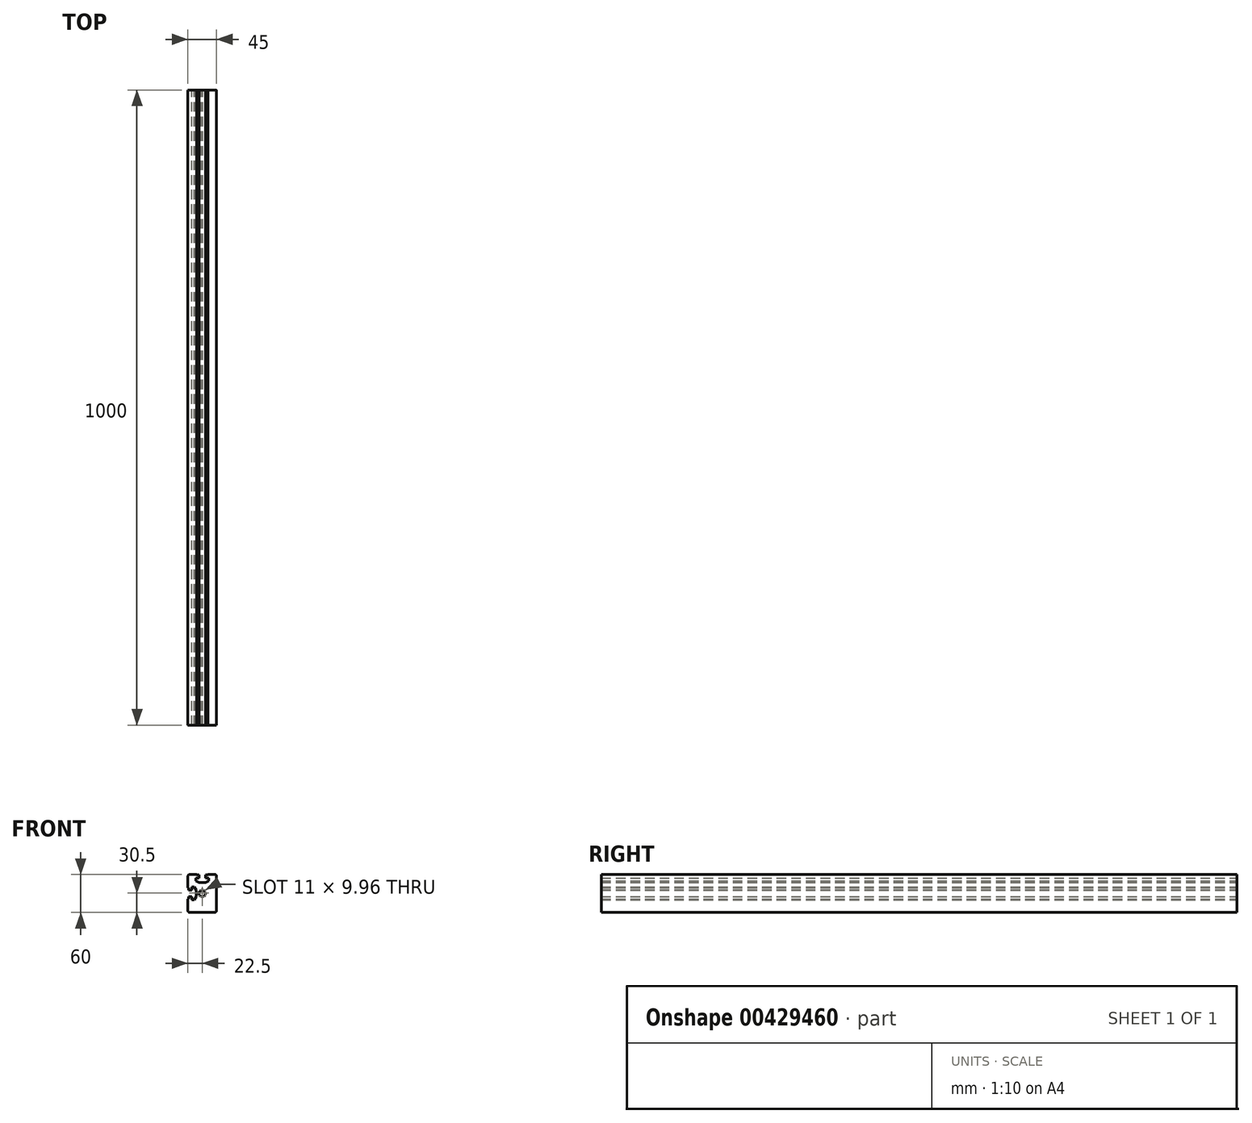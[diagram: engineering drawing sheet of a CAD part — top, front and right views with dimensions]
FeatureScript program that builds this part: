
annotation { "Feature Type Name" : "Feature", "Feature Type Description" : "" }
export const myFeature = defineFeature(function(context is Context, id is Id, definition is map)
    precondition{}
    {
        {
            var Q0;
            Q0=qCreatedBy(makeId("Front.planeOp"),FACE);
            var sketch = newSketch(context, id + "F0", { "sketchPlane" : qUnion([Q0])});
            skLineSegment(sketch, "E0.bottom", {"start": v(-22.5, 30) * mm, "end": v(22.5, 30) * mm});
            skLineSegment(sketch, "E0.top", {"start": v(-22.5, -30) * mm, "end": v(22.5, -30) * mm});
            skLineSegment(sketch, "E0.left", {"start": v(-22.5, 30) * mm, "end": v(-22.5, -30) * mm});
            skLineSegment(sketch, "E0.right", {"start": v(22.5, 30) * mm, "end": v(22.5, -30) * mm});
            skSolve(sketch);
        }
        {
            var Q0;
            Q0 = qSketchRegion(id + "F0", true);
            extrude(context, id + "F1", {"entities" : qUnion([Q0]), "depth" : 1000 * mm});
        }
        {
            var Q0;
            Q0=makeQuery(id+"F1.opExtrude","SWEPT_EDGE",EDGE,{"disambiguationData":[OSD([sQuery(id+"F0.wireOp",EDGE,"E0.top"),sQuery(id+"F0.wireOp",EDGE,"E0.left")])]});
            var Q1;
            Q1=makeQuery(id+"F1.opExtrude","SWEPT_EDGE",EDGE,{"disambiguationData":[OSD([sQuery(id+"F0.wireOp",EDGE,"E0.bottom"),sQuery(id+"F0.wireOp",EDGE,"E0.left")])]});
            var Q2;
            Q2=makeQuery(id+"F1.opExtrude","SWEPT_EDGE",EDGE,{"disambiguationData":[OSD([sQuery(id+"F0.wireOp",EDGE,"E0.top"),sQuery(id+"F0.wireOp",EDGE,"E0.right")])]});
            var Q3;
            Q3=makeQuery(id+"F1.opExtrude","SWEPT_EDGE",EDGE,{"disambiguationData":[OSD([sQuery(id+"F0.wireOp",EDGE,"E0.bottom"),sQuery(id+"F0.wireOp",EDGE,"E0.right")])]});
            fillet(context, id + "F2", {"entities" : qUnion([Q0, Q1, Q2, Q3]), "radius" : 3 * mm, "tangentPropagation" : true, "allowEdgeOverflow" : false});
        }
        {
            var Q0;
            Q0=qCreatedBy(makeId("Front.planeOp"),FACE);
            var sketch = newSketch(context, id + "F3", { "sketchPlane" : qUnion([Q0])});
            skCircle(sketch, "E1", {"center": v(0, 0) * mm, "radius": 5 * mm});
            skSolve(sketch);
        }
        {
            var Q0;
            Q0 = qSketchRegion(id + "F3", true);
            extrude(context, id + "F4", {"entities" : qUnion([Q0]), "operationType" : NewBodyOperationType.REMOVE, "endBound" : BoundingType.THROUGH_ALL, "depth" : 25 * mm});
        }
        {
            var Q0;
            Q0=qCreatedBy(makeId("Front.planeOp"),FACE);
            var sketch = newSketch(context, id + "F5", { "sketchPlane" : qUnion([Q0])});
            skLineSegment(sketch, "E2.bottom", {"start": v(-9, 30) * mm, "end": v(9, 30) * mm});
            skLineSegment(sketch, "E2.top", {"start": v(-9, 29) * mm, "end": v(-5, 29) * mm});
            skLineSegment(sketch, "E2.left", {"start": v(-9, 30) * mm, "end": v(-9, 29) * mm});
            skLineSegment(sketch, "E2.right", {"start": v(9, 30) * mm, "end": v(9, 29) * mm});
            skLineSegment(sketch, "E3.left", {"start": v(-5, 29) * mm, "end": v(-5, 24) * mm});
            skLineSegment(sketch, "E3.right", {"start": v(5, 29) * mm, "end": v(5, 24) * mm});
            skPoint(sketch, "E4.firstSnap0", {"position": v(0, 24) * mm});
            skLineSegment(sketch, "E4.bottom", {"start": v(-10.25, 24) * mm, "end": v(-5, 24) * mm});
            skLineSegment(sketch, "E4.top", {"start": v(-5.05, 17) * mm, "end": v(5.05, 17) * mm});
            skLineSegment(sketch, "E4.left", {"start": v(-10.25, 24) * mm, "end": v(-10.25, 20) * mm});
            skLineSegment(sketch, "E4.right", {"start": v(10.25, 24) * mm, "end": v(10.25, 20) * mm});
            skLineSegment(sketch, "E5.trimOffspring", {"start": v(5, 24) * mm, "end": v(10.25, 24) * mm});
            skLineSegment(sketch, "E6.trimOffspring", {"start": v(5, 29) * mm, "end": v(9, 29) * mm});
            skLineSegment(sketch, "E7", {"start": v(-10.25, 20) * mm, "end": v(-5.05, 17) * mm});
            skLineSegment(sketch, "E8", {"start": v(5.05, 17) * mm, "end": v(10.25, 20) * mm});
            skSolve(sketch);
        }
        {
            var Q0;
            Q0 = qSketchRegion(id + "F5", true);
            extrude(context, id + "F6", {"entities" : qUnion([Q0]), "operationType" : NewBodyOperationType.REMOVE, "endBound" : BoundingType.THROUGH_ALL, "depth" : 25 * mm});
        }
        {
            var Q0;
            Q0=qCreatedBy(makeId("Front.planeOp"),FACE);
            var sketch = newSketch(context, id + "F7", { "sketchPlane" : qUnion([Q0])});
            skLineSegment(sketch, "E9.bottom", {"start": v(-22.5, 9) * mm, "end": v(-21.5, 9) * mm});
            skLineSegment(sketch, "E9.top", {"start": v(-22.5, -9) * mm, "end": v(-21.5, -9) * mm});
            skLineSegment(sketch, "E9.left", {"start": v(-22.5, 9) * mm, "end": v(-22.5, -9) * mm});
            skLineSegment(sketch, "E9.right", {"start": v(-21.5, 9) * mm, "end": v(-21.5, 5) * mm});
            skLineSegment(sketch, "E10.bottom", {"start": v(-21.5, 5) * mm, "end": v(-16.5, 5) * mm});
            skLineSegment(sketch, "E10.top", {"start": v(-21.5, -5) * mm, "end": v(-16.5, -5) * mm});
            skLineSegment(sketch, "E11.bottom", {"start": v(-16.5, 10.25) * mm, "end": v(-12.5, 10.25) * mm});
            skLineSegment(sketch, "E11.top", {"start": v(-16.5, -10.25) * mm, "end": v(-12.5, -10.25) * mm});
            skLineSegment(sketch, "E11.left", {"start": v(-16.5, 10.25) * mm, "end": v(-16.5, 5) * mm});
            skLineSegment(sketch, "E11.right", {"start": v(-9.5, 5.05) * mm, "end": v(-9.5, -5.05) * mm});
            skLineSegment(sketch, "E12.trimOffspring", {"start": v(-16.5, -5) * mm, "end": v(-16.5, -10.25) * mm});
            skLineSegment(sketch, "E13.trimOffspring", {"start": v(-21.5, -5) * mm, "end": v(-21.5, -9) * mm});
            skLineSegment(sketch, "E14", {"start": v(-12.5, 10.25) * mm, "end": v(-9.5, 5.05) * mm});
            skLineSegment(sketch, "E15", {"start": v(-9.5, -5.05) * mm, "end": v(-12.5, -10.25) * mm});
            skSolve(sketch);
        }
        {
            var Q0;
            Q0 = qSketchRegion(id + "F7", true);
            extrude(context, id + "F8", {"entities" : qUnion([Q0]), "operationType" : NewBodyOperationType.REMOVE, "endBound" : BoundingType.THROUGH_ALL, "depth" : 25 * mm});
        }
        {
            var Q0;
            Q0=qCreatedBy(makeId("Front.planeOp"),FACE);
            var sketch = newSketch(context, id + "F9", { "sketchPlane" : qUnion([Q0])});
            skArc(sketch, "E16", {"start": v(1.04, 5.9) * mm, "mid": v(0, 6) * mm, "end": v(-1.04, 5.9) * mm});
            skLineSegment(sketch, "E17", {"start": v(-1.04, 5.9) * mm, "end": v(0, 0) * mm});
            skLineSegment(sketch, "E18", {"start": v(0, 0) * mm, "end": v(1.04, 5.9) * mm});
            skSolve(sketch);
        }
        {
            var Q0;
            Q0 = qSketchRegion(id + "F9", true);
            extrude(context, id + "F10", {"entities" : qUnion([Q0]), "operationType" : NewBodyOperationType.REMOVE, "endBound" : BoundingType.THROUGH_ALL, "depth" : 25 * mm});
        }
    });
